# Revit family: Air Terminals_Abmessungen DIA KLFL Anschlussart „Klemmflansch“_rund
name_source: partatom
category: Air Terminals
revit_build: Autodesk Revit 2017 (Build: 20160225_1515(x64)
units: mm (PartAtom-declared; Revit-internal decimal feet)

## family parameters
Always vertical = Yes
Cut with Voids When Loaded = No
Part Type = Normal
Room Calculation Point = No
Round Connector Dimension = Use Diameter
Shared = No
Work Plane-Based = No

## types (4) — shared parameters
LWA dB(A) = 30,35,40
Maß □ D = 620 mm  [stored 2.03412 ft]

## per-type parameters (varying)
| type | DN 250 | DN 315 | DN 355 | Index | Maß C | Maß Ø D | Maß Ø E | Maß Ø F | Maß Ø d | Mindestabstand m | V˙0 m3/ h | xkrit m | ∆p Pa |
| DN 180 | No | No | No | 1 | 119 mm  [stored 0.39042 ft] | 284 mm  [stored 0.931759 ft] | 226 mm  [stored 0.74147 ft] | 255 mm  [stored 0.836614 ft] | 158 mm | 1.3,2.0,3.1 | 140,170,200 | 1.8,2.2,2.6 | 20,29,40 |
| DN 250 | Yes | No | No | 2 | 143 mm | 384 mm  [stored 1.25984 ft] | 311 mm  [stored 1.02034 ft] | 340 mm  [stored 1.11549 ft] | 198 mm  [stored 0.649606 ft] | 3.3,4.6,6.0 | 250,290,340 | 1.6,1.9,2.2 | 20,26,37 |
| DN 315 | Yes | Yes | No | 3 | 169 mm  [stored 0.554462 ft] | 494 mm | 400 mm  [stored 1.31234 ft] | 429 mm  [stored 1.40748 ft] | 248 mm  [stored 0.813648 ft] | 5.1,6.8,8.8 | 350,410,490 | 1.3,1.6,2.0 | 18,25,37 |
| DN 355 | Yes | Yes | Yes | 4 | 185 mm  [stored 0.606955 ft] | 554 mm  [stored 1.81759 ft] | 448 mm  [stored 1.46982 ft] | 478 mm  [stored 1.56824 ft] | 278 mm  [stored 0.912073 ft] | 6.7,8.6,11.0 | 410,480,540 | 1.4,1.6,2.0 | 17,23,29 |

note: [stored X ft] marks values corroborated as IEEE doubles in the binary element streams (Revit-internal decimal feet)

## geometry (parser evidence)
native form markers: Sweep x55
no freeform markers — native parametric forms only
